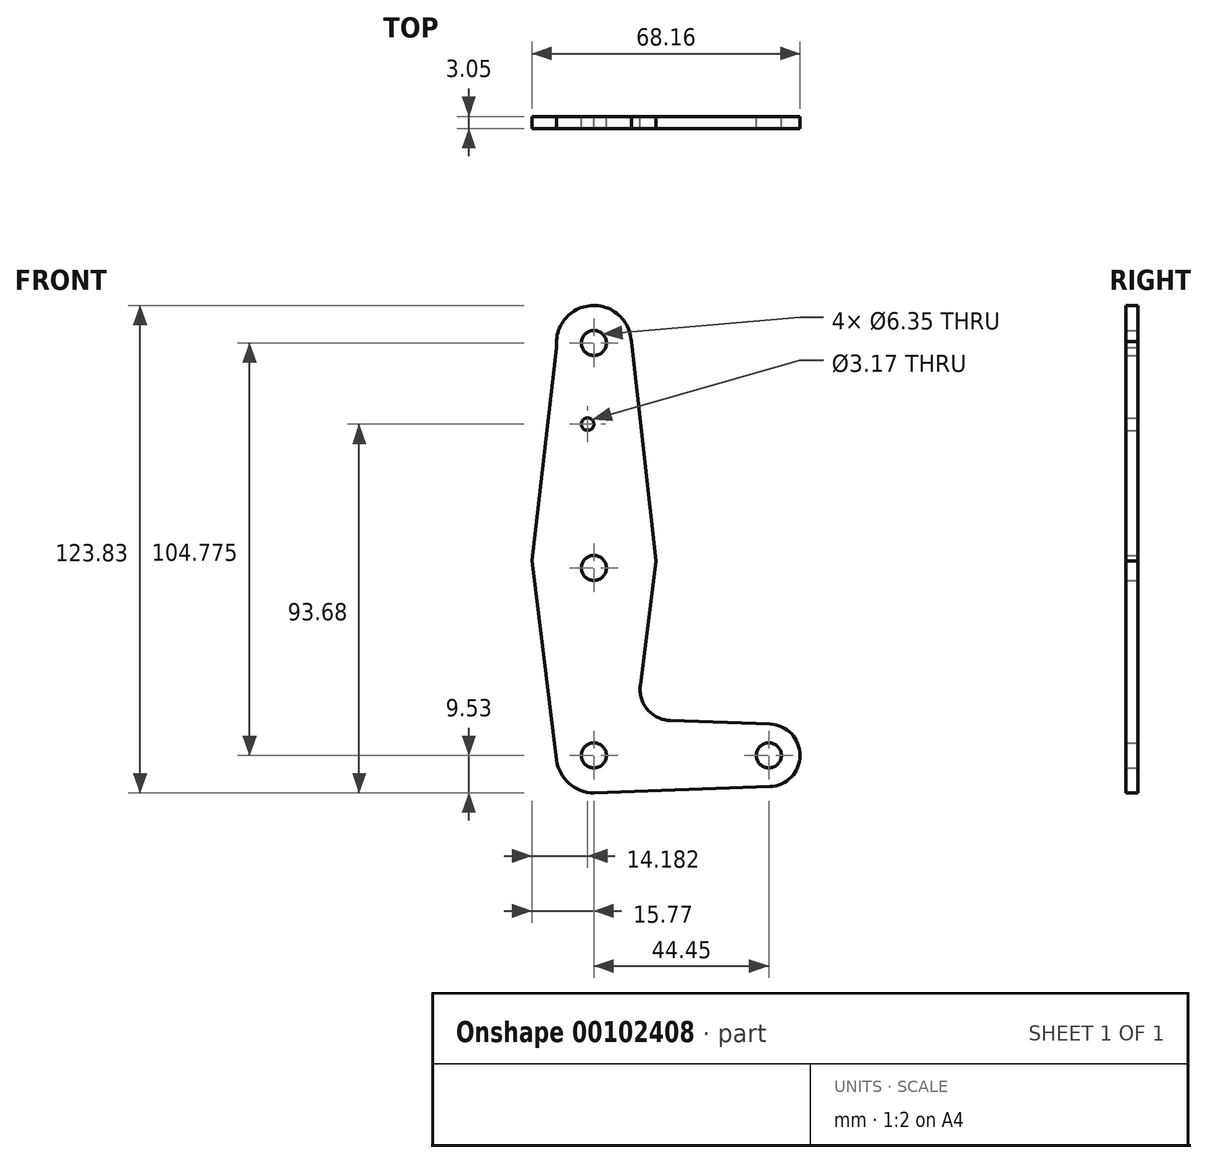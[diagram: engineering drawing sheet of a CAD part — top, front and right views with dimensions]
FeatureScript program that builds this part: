
annotation { "Feature Type Name" : "Feature", "Feature Type Description" : "" }
export const myFeature = defineFeature(function(context is Context, id is Id, definition is map)
    precondition{}
    {
        {
            var Q0;
            Q0=qCreatedBy(makeId("Front.planeOp"),FACE);
            var sketch = newSketch(context, id + "F0", { "sketchPlane" : qUnion([Q0])});
            skLineSegment(sketch, "E0", {"start": v(0, 104.78) * mm, "end": v(0, 0) * mm, "construction": true});
            skLineSegment(sketch, "E1", {"start": v(0, 0) * mm, "end": v(44.45, 0) * mm, "construction": true});
            skCircle(sketch, "E2", {"center": v(0, 104.78) * mm, "radius": 9.53 * mm});
            skCircle(sketch, "E3", {"center": v(0, 47.62) * mm, "radius": 15.88 * mm});
            skCircle(sketch, "E4", {"center": v(0, 0) * mm, "radius": 9.53 * mm});
            skCircle(sketch, "E5", {"center": v(44.45, 0) * mm, "radius": 7.94 * mm});
            skLineSegment(sketch, "E6", {"start": v(-9.46, 103.63) * mm, "end": v(-15.77, 49.46) * mm});
            skLineSegment(sketch, "E7", {"start": v(9.52, 105.19) * mm, "end": v(15.78, 49.4) * mm});
            skLineSegment(sketch, "E8", {"start": v(-15.77, 49.46) * mm, "end": v(-9.45, -1.18) * mm});
            skLineSegment(sketch, "E9", {"start": v(15.78, 49.4) * mm, "end": v(11.82, 17.77) * mm});
            skLineSegment(sketch, "E10", {"start": v(19.43, 8.83) * mm, "end": v(44.73, 7.93) * mm});
            skLineSegment(sketch, "E11", {"start": v(0, -9.53) * mm, "end": v(44.73, -7.93) * mm});
            skCircle(sketch, "E12", {"center": v(0, 104.78) * mm, "radius": 3.18 * mm});
            skCircle(sketch, "E13", {"center": v(0, 47.62) * mm, "radius": 3.18 * mm});
            skCircle(sketch, "E14", {"center": v(0, 0) * mm, "radius": 3.18 * mm});
            skCircle(sketch, "E15", {"center": v(44.45, 0) * mm, "radius": 3.18 * mm});
            skCircle(sketch, "E16", {"center": v(-1.59, 84.15) * mm, "radius": 1.59 * mm});
            skArc(sketch, "E17.filletArc", {"start": v(11.82, 17.77) * mm, "mid": v(13.66, 11.62) * mm, "end": v(19.43, 8.83) * mm});
            skSolve(sketch);
        }
        {
            var Q0;
            Q0=makeQuery(id+"F0.imprint","IMPRINT",FACE,{"disambiguationData":[TD([[makeQuery(id+"F0.imprint","IMPRINT",EDGE,{"derivedFrom":sQuery(id+"F0.wireOp",EDGE,"E12")}),-1.0]])]});
            var Q1;
            {var subQ9=sQuery(id+"F0.wireOp",EDGE,"E10");Q1=makeQuery(id+"F0.imprint","IMPRINT",FACE,{"disambiguationData":[TD([[makeQuery(id+"F0.imprint","IMPRINT",EDGE,{"derivedFrom":subQ9}),-1.0]])]});}
            var Q2;
            {var subQ1=sQuery(id+"F0.wireOp",EDGE,"E6");Q2=makeQuery(id+"F0.imprint","IMPRINT",FACE,{"disambiguationData":[TD([[makeQuery(id+"F0.imprint","IMPRINT",EDGE,{"derivedFrom":subQ1}),1.0]])]});}
            var Q3;
            Q3=makeQuery(id+"F0.imprint","IMPRINT",FACE,{"disambiguationData":[TD([[makeQuery(id+"F0.imprint","IMPRINT",EDGE,{"derivedFrom":sQuery(id+"F0.wireOp",EDGE,"E13")}),-1.0]])]});
            var Q4;
            Q4=makeQuery(id+"F0.imprint","IMPRINT",FACE,{"disambiguationData":[TD([[makeQuery(id+"F0.imprint","IMPRINT",EDGE,{"derivedFrom":sQuery(id+"F0.wireOp",EDGE,"E14")}),-1.0]])]});
            var Q5;
            Q5=makeQuery(id+"F0.imprint","IMPRINT",FACE,{"disambiguationData":[TD([[makeQuery(id+"F0.imprint","IMPRINT",EDGE,{"derivedFrom":sQuery(id+"F0.wireOp",EDGE,"E15")}),-1.0]])]});
            extrude(context, id + "F1", {"entities" : qUnion([Q0, Q1, Q2, Q3, Q4, Q5]), "depth" : 3.05 * mm});
        }
    });
